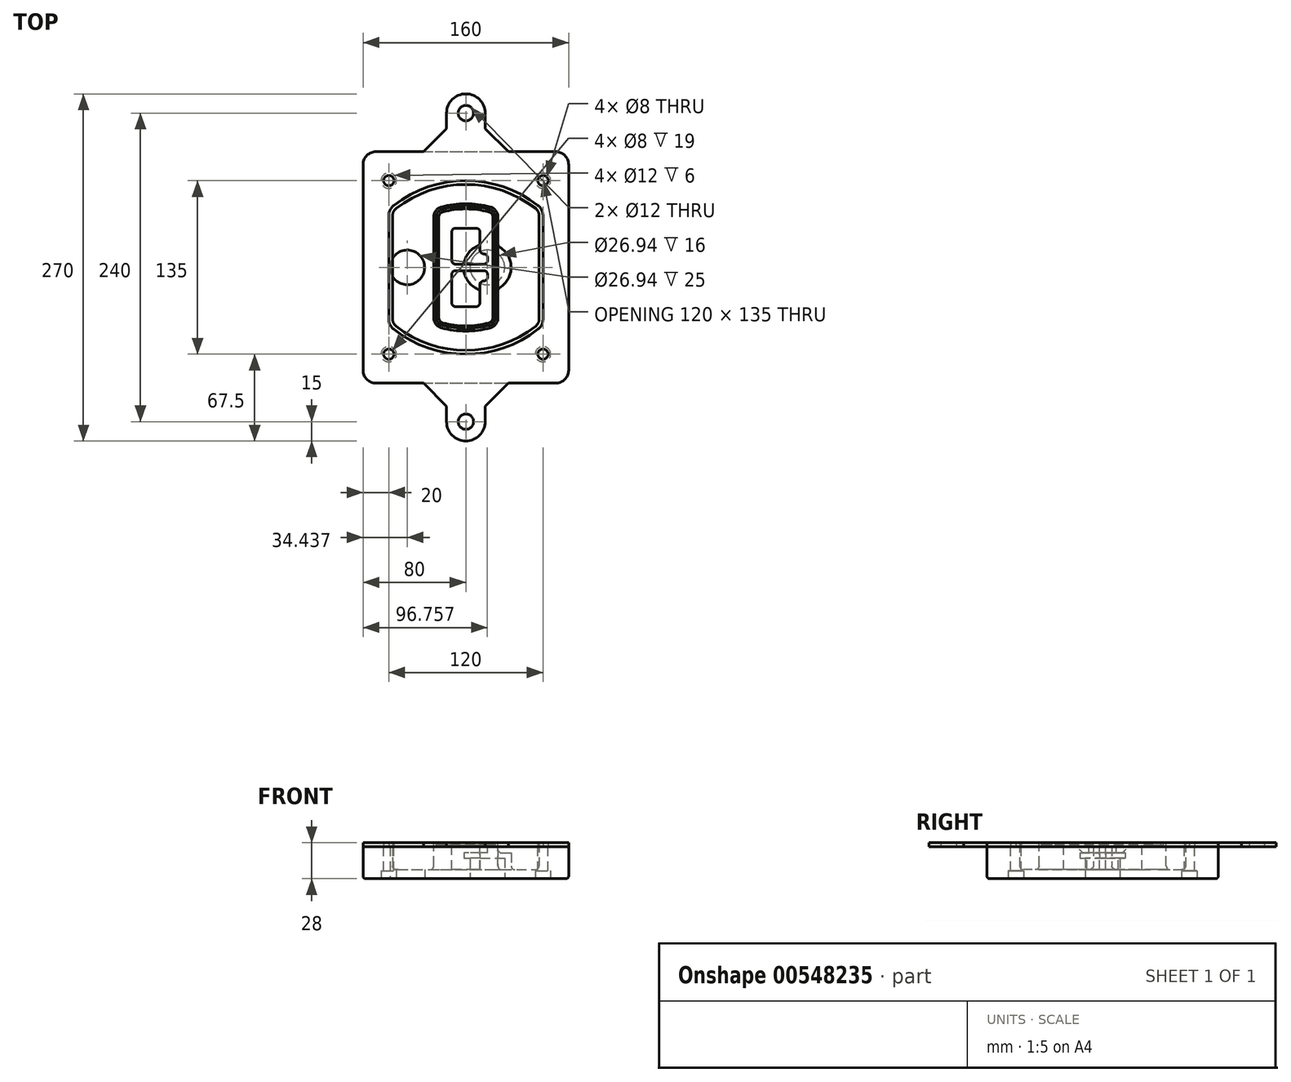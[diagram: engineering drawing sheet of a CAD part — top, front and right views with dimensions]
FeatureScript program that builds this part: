
annotation { "Feature Type Name" : "Feature", "Feature Type Description" : "" }
export const myFeature = defineFeature(function(context is Context, id is Id, definition is map)
    precondition{}
    {
        {
            var Q0;
            Q0=qCreatedBy(makeId("Top.planeOp"),FACE);
            var sketch = newSketch(context, id + "F0", { "sketchPlane" : qUnion([Q0])});
            skPoint(sketch, "E0.rect.middle", {"position": v(0, 0) * mm});
            skLineSegment(sketch, "E1.bottom", {"start": v(-70, -90) * mm, "end": v(70, -90) * mm});
            skLineSegment(sketch, "E1.top", {"start": v(-70, 90) * mm, "end": v(70, 90) * mm});
            skLineSegment(sketch, "E1.left", {"start": v(-80, -80) * mm, "end": v(-80, 80) * mm});
            skLineSegment(sketch, "E1.right", {"start": v(80, -80) * mm, "end": v(80, 80) * mm});
            skLineSegment(sketch, "E2", {"start": v(-80, 90) * mm, "end": v(80, -90) * mm, "construction": true});
            skLineSegment(sketch, "E3", {"start": v(80, 90) * mm, "end": v(-80, -90) * mm, "construction": true});
            skCircle(sketch, "E4", {"center": v(-60, 67.5) * mm, "radius": 4 * mm});
            skCircle(sketch, "E5", {"center": v(60, 67.5) * mm, "radius": 4 * mm});
            skCircle(sketch, "E6", {"center": v(60, -67.5) * mm, "radius": 4 * mm});
            skCircle(sketch, "E7", {"center": v(-60, -67.5) * mm, "radius": 4 * mm});
            skLineSegment(sketch, "E8", {"start": v(-60, 67.5) * mm, "end": v(60, 67.5) * mm, "construction": true});
            skLineSegment(sketch, "E9", {"start": v(60, 67.5) * mm, "end": v(60, -67.5) * mm, "construction": true});
            skLineSegment(sketch, "E10", {"start": v(60, -67.5) * mm, "end": v(-60, -67.5) * mm, "construction": true});
            skLineSegment(sketch, "E11", {"start": v(-60, -67.5) * mm, "end": v(-60, 67.5) * mm, "construction": true});
            skLineSegment(sketch, "E12", {"start": v(-60, 40.3) * mm, "end": v(-60, -40.3) * mm});
            skLineSegment(sketch, "E13", {"start": v(60, 40.3) * mm, "end": v(60, -40.3) * mm});
            skArc(sketch, "E14", {"start": v(56.15, 48.18) * mm, "mid": v(0, 67.5) * mm, "end": v(-56.15, 48.18) * mm});
            skArc(sketch, "E15", {"start": v(-56.15, -48.18) * mm, "mid": v(0, -67.5) * mm, "end": v(56.15, -48.18) * mm});
            skLineSegment(sketch, "E16", {"start": v(-60, 0) * mm, "end": v(60, 0) * mm, "construction": true});
            skPoint(sketch, "E17.visualSharp", {"position": v(-60, -45) * mm});
            skArc(sketch, "E17.filletArc", {"start": v(-60, -40.3) * mm, "mid": v(-58.99, -44.68) * mm, "end": v(-56.15, -48.18) * mm});
            skPoint(sketch, "E18.visualSharp", {"position": v(-60, 45) * mm});
            skArc(sketch, "E18.filletArc", {"start": v(-56.15, 48.18) * mm, "mid": v(-58.99, 44.68) * mm, "end": v(-60, 40.3) * mm});
            skPoint(sketch, "E19.visualSharp", {"position": v(60, 45) * mm});
            skArc(sketch, "E19.filletArc", {"start": v(60, 40.3) * mm, "mid": v(58.99, 44.68) * mm, "end": v(56.15, 48.18) * mm});
            skPoint(sketch, "E20.visualSharp", {"position": v(60, -45) * mm});
            skArc(sketch, "E20.filletArc", {"start": v(56.15, -48.18) * mm, "mid": v(58.99, -44.68) * mm, "end": v(60, -40.3) * mm});
            skPoint(sketch, "E21.visualSharp", {"position": v(-80, 90) * mm});
            skArc(sketch, "E21.filletArc", {"start": v(-70, 90) * mm, "mid": v(-77.07, 87.07) * mm, "end": v(-80, 80) * mm});
            skPoint(sketch, "E22.visualSharp", {"position": v(80, 90) * mm});
            skArc(sketch, "E22.filletArc", {"start": v(80, 80) * mm, "mid": v(77.07, 87.07) * mm, "end": v(70, 90) * mm});
            skPoint(sketch, "E23.visualSharp", {"position": v(80, -90) * mm});
            skArc(sketch, "E23.filletArc", {"start": v(70, -90) * mm, "mid": v(77.07, -87.07) * mm, "end": v(80, -80) * mm});
            skPoint(sketch, "E24.visualSharp", {"position": v(-80, -90) * mm});
            skArc(sketch, "E24.filletArc", {"start": v(-80, -80) * mm, "mid": v(-77.07, -87.07) * mm, "end": v(-70, -90) * mm});
            skArc(sketch, "E25.0", {"start": v(57, 40.3) * mm, "mid": v(56.3, 43.36) * mm, "end": v(54.3, 45.81) * mm});
            skLineSegment(sketch, "E25.1", {"start": v(57, 40.3) * mm, "end": v(57, -40.3) * mm});
            skArc(sketch, "E25.2", {"start": v(54.3, -45.81) * mm, "mid": v(56.3, -43.36) * mm, "end": v(57, -40.3) * mm});
            skArc(sketch, "E25.3", {"start": v(-54.3, -45.81) * mm, "mid": v(0, -64.5) * mm, "end": v(54.3, -45.81) * mm});
            skArc(sketch, "E25.4", {"start": v(-57, -40.3) * mm, "mid": v(-56.3, -43.36) * mm, "end": v(-54.3, -45.81) * mm});
            skArc(sketch, "E25.5", {"start": v(54.3, 45.81) * mm, "mid": v(0, 64.5) * mm, "end": v(-54.3, 45.81) * mm});
            skLineSegment(sketch, "E25.6", {"start": v(-57, 40.3) * mm, "end": v(-57, -40.3) * mm});
            skArc(sketch, "E25.7", {"start": v(-54.3, 45.81) * mm, "mid": v(-56.3, 43.36) * mm, "end": v(-57, 40.3) * mm});
            skArc(sketch, "E26.0", {"start": v(-58.62, 51.33) * mm, "mid": v(-62.58, 46.43) * mm, "end": v(-64, 40.3) * mm});
            skArc(sketch, "E26.1", {"start": v(58.62, 51.33) * mm, "mid": v(0, 71.5) * mm, "end": v(-58.62, 51.33) * mm});
            skArc(sketch, "E26.2", {"start": v(64, 40.3) * mm, "mid": v(62.58, 46.43) * mm, "end": v(58.62, 51.33) * mm});
            skLineSegment(sketch, "E26.3", {"start": v(64, 40.3) * mm, "end": v(64, -40.3) * mm});
            skArc(sketch, "E26.4", {"start": v(58.62, -51.33) * mm, "mid": v(62.58, -46.43) * mm, "end": v(64, -40.3) * mm});
            skLineSegment(sketch, "E26.5", {"start": v(-64, 40.3) * mm, "end": v(-64, -40.3) * mm});
            skArc(sketch, "E26.6", {"start": v(-58.62, -51.33) * mm, "mid": v(0, -71.5) * mm, "end": v(58.62, -51.33) * mm});
            skArc(sketch, "E26.7", {"start": v(-64, -40.3) * mm, "mid": v(-62.58, -46.43) * mm, "end": v(-58.62, -51.33) * mm});
            skSolve(sketch);
        }
        {
            var Q0;
            Q0=makeQuery(id+"F0.imprint","IMPRINT",FACE,{"disambiguationData":[TD([[makeQuery(id+"F0.imprint","IMPRINT",EDGE,{"derivedFrom":sQuery(id+"F0.wireOp",EDGE,"E1.bottom")}),1.0]])]});
            var Q1;
            Q1=makeQuery(id+"F0.imprint","IMPRINT",FACE,{"disambiguationData":[TD([[makeQuery(id+"F0.imprint","IMPRINT",EDGE,{"derivedFrom":sQuery(id+"F0.wireOp",EDGE,"E12")}),1.0]])]});
            var Q2;
            Q2=makeQuery(id+"F0.imprint","IMPRINT",FACE,{"disambiguationData":[TD([[makeQuery(id+"F0.imprint","IMPRINT",EDGE,{"derivedFrom":sQuery(id+"F0.wireOp",EDGE,"E25.0")}),1.0]])]});
            var Q3;
            Q3=makeQuery(id+"F0.imprint","IMPRINT",FACE,{"disambiguationData":[TD([[makeQuery(id+"F0.imprint","IMPRINT",EDGE,{"derivedFrom":sQuery(id+"F0.wireOp",EDGE,"E12")}),-1.0]])]});
            extrude(context, id + "F1", {"entities" : qUnion([Q0, Q1, Q2, Q3]), "oppositeDirection" : true, "depth" : 25 * mm});
        }
        {
            var Q0;
            Q0=makeQuery(id+"F0.imprint","IMPRINT",FACE,{"disambiguationData":[TD([[makeQuery(id+"F0.imprint","IMPRINT",EDGE,{"derivedFrom":sQuery(id+"F0.wireOp",EDGE,"E12")}),1.0]])]});
            extrude(context, id + "F2", {"entities" : qUnion([Q0]), "operationType" : NewBodyOperationType.ADD, "depth" : 3 * mm});
        }
        {
            var Q0;
            Q0=makeQuery(id+"F0.imprint","IMPRINT",FACE,{"disambiguationData":[TD([[makeQuery(id+"F0.imprint","IMPRINT",EDGE,{"derivedFrom":sQuery(id+"F0.wireOp",EDGE,"E25.0")}),1.0]])]});
            extrude(context, id + "F3", {"entities" : qUnion([Q0]), "operationType" : NewBodyOperationType.REMOVE, "oppositeDirection" : true, "depth" : 18 * mm});
        }
        {
            var Q0;
            Q0=makeQuery(id+"F2.opExtrude","CAP_FACE",FACE,{"disambiguationData":[OSD([sQuery(id+"F0.wireOp",EDGE,"E12"),sQuery(id+"F0.wireOp",EDGE,"E13"),sQuery(id+"F0.wireOp",EDGE,"E14"),sQuery(id+"F0.wireOp",EDGE,"E15"),sQuery(id+"F0.wireOp",EDGE,"E17.filletArc"),sQuery(id+"F0.wireOp",EDGE,"E18.filletArc"),sQuery(id+"F0.wireOp",EDGE,"E19.filletArc"),sQuery(id+"F0.wireOp",EDGE,"E20.filletArc"),sQuery(id+"F0.wireOp",EDGE,"E25.0"),sQuery(id+"F0.wireOp",EDGE,"E25.1"),sQuery(id+"F0.wireOp",EDGE,"E25.2"),sQuery(id+"F0.wireOp",EDGE,"E25.3"),sQuery(id+"F0.wireOp",EDGE,"E25.4"),sQuery(id+"F0.wireOp",EDGE,"E25.5"),sQuery(id+"F0.wireOp",EDGE,"E25.6"),sQuery(id+"F0.wireOp",EDGE,"E25.7")])],"isStart":false});
            var sketch = newSketch(context, id + "F4", { "sketchPlane" : qUnion([Q0])});
            skArc(sketch, "E27.0", {"start": v(-19.08, -46.97) * mm, "mid": v(0, -49.5) * mm, "end": v(19.08, -46.97) * mm});
            skArc(sketch, "E28.0", {"start": v(19.08, 46.97) * mm, "mid": v(0, 49.5) * mm, "end": v(-19.08, 46.97) * mm});
            skLineSegment(sketch, "E29", {"start": v(-25, 39.25) * mm, "end": v(-25, -39.25) * mm});
            skLineSegment(sketch, "E30", {"start": v(25, 39.25) * mm, "end": v(25, -39.25) * mm});
            skLineSegment(sketch, "E31", {"start": v(-25, 45.1) * mm, "end": v(25, 45.1) * mm, "construction": true});
            skLineSegment(sketch, "E32", {"start": v(-25, -45.1) * mm, "end": v(25, -45.1) * mm, "construction": true});
            skPoint(sketch, "E33.visualSharp", {"position": v(-25, 45.1) * mm});
            skArc(sketch, "E33.filletArc", {"start": v(-19.08, 46.97) * mm, "mid": v(-23.35, 44.11) * mm, "end": v(-25, 39.25) * mm});
            skPoint(sketch, "E34.visualSharp", {"position": v(25, 45.1) * mm});
            skArc(sketch, "E34.filletArc", {"start": v(25, 39.25) * mm, "mid": v(23.35, 44.11) * mm, "end": v(19.08, 46.97) * mm});
            skPoint(sketch, "E35.visualSharp", {"position": v(25, -45.1) * mm});
            skArc(sketch, "E35.filletArc", {"start": v(19.08, -46.97) * mm, "mid": v(23.35, -44.11) * mm, "end": v(25, -39.25) * mm});
            skPoint(sketch, "E36.visualSharp", {"position": v(-25, -45.1) * mm});
            skArc(sketch, "E36.filletArc", {"start": v(-25, -39.25) * mm, "mid": v(-23.35, -44.11) * mm, "end": v(-19.08, -46.97) * mm});
            skArc(sketch, "E37.0", {"start": v(54.3, 45.81) * mm, "mid": v(0, 64.5) * mm, "end": v(-54.3, 45.81) * mm});
            skArc(sketch, "E37.1", {"start": v(-54.3, 45.81) * mm, "mid": v(-56.3, 43.36) * mm, "end": v(-57, 40.3) * mm});
            skLineSegment(sketch, "E37.2", {"start": v(-57, 40.3) * mm, "end": v(-57, -40.3) * mm});
            skArc(sketch, "E37.3", {"start": v(-57, -40.3) * mm, "mid": v(-56.3, -43.36) * mm, "end": v(-54.3, -45.81) * mm});
            skArc(sketch, "E37.4", {"start": v(-54.3, -45.81) * mm, "mid": v(0, -64.5) * mm, "end": v(54.3, -45.81) * mm});
            skArc(sketch, "E37.5", {"start": v(54.3, -45.81) * mm, "mid": v(56.3, -43.36) * mm, "end": v(57, -40.3) * mm});
            skLineSegment(sketch, "E37.6", {"start": v(57, 40.3) * mm, "end": v(57, -40.3) * mm});
            skArc(sketch, "E37.7", {"start": v(57, 40.3) * mm, "mid": v(56.3, 43.36) * mm, "end": v(54.3, 45.81) * mm});
            skLineSegment(sketch, "E38.0", {"start": v(23, 39.25) * mm, "end": v(23, -39.25) * mm});
            skArc(sketch, "E38.1", {"start": v(18.56, -45.04) * mm, "mid": v(21.76, -42.9) * mm, "end": v(23, -39.25) * mm});
            skArc(sketch, "E38.2", {"start": v(-18.56, -45.04) * mm, "mid": v(0, -47.5) * mm, "end": v(18.56, -45.04) * mm});
            skArc(sketch, "E38.3", {"start": v(-23, -39.25) * mm, "mid": v(-21.76, -42.9) * mm, "end": v(-18.56, -45.04) * mm});
            skLineSegment(sketch, "E38.4", {"start": v(-23, 39.25) * mm, "end": v(-23, -39.25) * mm});
            skArc(sketch, "E38.5", {"start": v(23, 39.25) * mm, "mid": v(21.76, 42.9) * mm, "end": v(18.56, 45.04) * mm});
            skArc(sketch, "E38.6", {"start": v(-18.56, 45.04) * mm, "mid": v(-21.76, 42.9) * mm, "end": v(-23, 39.25) * mm});
            skArc(sketch, "E38.7", {"start": v(18.56, 45.04) * mm, "mid": v(0, 47.5) * mm, "end": v(-18.56, 45.04) * mm});
            skArc(sketch, "E39.0", {"start": v(21, 39.25) * mm, "mid": v(20.18, 41.68) * mm, "end": v(18.04, 43.1) * mm});
            skLineSegment(sketch, "E39.1", {"start": v(21, 39.25) * mm, "end": v(21, -39.25) * mm});
            skArc(sketch, "E39.2", {"start": v(18.04, -43.1) * mm, "mid": v(20.18, -41.68) * mm, "end": v(21, -39.25) * mm});
            skArc(sketch, "E39.3", {"start": v(-18.04, -43.1) * mm, "mid": v(0, -45.5) * mm, "end": v(18.04, -43.1) * mm});
            skArc(sketch, "E39.4", {"start": v(-21, -39.25) * mm, "mid": v(-20.18, -41.68) * mm, "end": v(-18.04, -43.1) * mm});
            skArc(sketch, "E39.5", {"start": v(18.04, 43.1) * mm, "mid": v(0, 45.5) * mm, "end": v(-18.04, 43.1) * mm});
            skLineSegment(sketch, "E39.6", {"start": v(-21, 39.25) * mm, "end": v(-21, -39.25) * mm});
            skArc(sketch, "E39.7", {"start": v(-18.04, 43.1) * mm, "mid": v(-20.18, 41.68) * mm, "end": v(-21, 39.25) * mm});
            skLineSegment(sketch, "E40", {"start": v(-25, 0) * mm, "end": v(25, 0) * mm, "construction": true});
            skLineSegment(sketch, "E41", {"start": v(-11, 5.5) * mm, "end": v(-11, 27.5) * mm});
            skLineSegment(sketch, "E42", {"start": v(-8, 30.5) * mm, "end": v(8, 30.5) * mm});
            skLineSegment(sketch, "E43", {"start": v(11, 27.5) * mm, "end": v(11, 13.5) * mm});
            skLineSegment(sketch, "E44", {"start": v(14, 10.5) * mm, "end": v(14, 10.5) * mm});
            skLineSegment(sketch, "E45", {"start": v(17, 7.5) * mm, "end": v(17, 5.5) * mm});
            skLineSegment(sketch, "E46", {"start": v(14, 2.5) * mm, "end": v(-8, 2.5) * mm});
            skPoint(sketch, "E47.visualSharp", {"position": v(-11, 30.5) * mm});
            skArc(sketch, "E47.filletArc", {"start": v(-8, 30.5) * mm, "mid": v(-10.12, 29.62) * mm, "end": v(-11, 27.5) * mm});
            skPoint(sketch, "E48.visualSharp", {"position": v(11, 30.5) * mm});
            skArc(sketch, "E48.filletArc", {"start": v(11, 27.5) * mm, "mid": v(10.12, 29.62) * mm, "end": v(8, 30.5) * mm});
            skPoint(sketch, "E49.visualSharp", {"position": v(11, 10.5) * mm});
            skArc(sketch, "E49.filletArc", {"start": v(11, 13.5) * mm, "mid": v(11.88, 11.38) * mm, "end": v(14, 10.5) * mm});
            skPoint(sketch, "E50.visualSharp", {"position": v(17, 10.5) * mm});
            skArc(sketch, "E50.filletArc", {"start": v(17, 7.5) * mm, "mid": v(16.12, 9.62) * mm, "end": v(14, 10.5) * mm});
            skPoint(sketch, "E51.visualSharp", {"position": v(17, 2.5) * mm});
            skArc(sketch, "E51.filletArc", {"start": v(14, 2.5) * mm, "mid": v(16.12, 3.38) * mm, "end": v(17, 5.5) * mm});
            skPoint(sketch, "E52.visualSharp", {"position": v(-11, 2.5) * mm});
            skArc(sketch, "E52.filletArc", {"start": v(-11, 5.5) * mm, "mid": v(-10.12, 3.38) * mm, "end": v(-8, 2.5) * mm});
            skLineSegment(sketch, "E53.0.MirrorCS", {"start": v(14, -2.5) * mm, "end": v(-8, -2.5) * mm});
            skArc(sketch, "E54.0.MirrorCS", {"start": v(-11, -5.5) * mm, "mid": v(-10.12, -3.38) * mm, "end": v(-8, -2.5) * mm});
            skLineSegment(sketch, "E55.0.MirrorCS", {"start": v(-11, -5.5) * mm, "end": v(-11, -27.5) * mm});
            skArc(sketch, "E56.0.MirrorCS", {"start": v(-8, -30.5) * mm, "mid": v(-10.12, -29.62) * mm, "end": v(-11, -27.5) * mm});
            skLineSegment(sketch, "E57.0.MirrorCS", {"start": v(-8, -30.5) * mm, "end": v(8, -30.5) * mm});
            skArc(sketch, "E58.0.MirrorCS", {"start": v(11, -27.5) * mm, "mid": v(10.12, -29.62) * mm, "end": v(8, -30.5) * mm});
            skLineSegment(sketch, "E59.0.MirrorCS", {"start": v(11, -27.5) * mm, "end": v(11, -13.5) * mm});
            skArc(sketch, "E60.0.MirrorCS", {"start": v(11, -13.5) * mm, "mid": v(11.88, -11.38) * mm, "end": v(14, -10.5) * mm});
            skArc(sketch, "E61.0.MirrorCS", {"start": v(17, -7.5) * mm, "mid": v(16.12, -9.62) * mm, "end": v(14, -10.5) * mm});
            skLineSegment(sketch, "E62.0.MirrorCS", {"start": v(17, -7.5) * mm, "end": v(17, -5.5) * mm});
            skArc(sketch, "E63.0.MirrorCS", {"start": v(14, -2.5) * mm, "mid": v(16.12, -3.38) * mm, "end": v(17, -5.5) * mm});
            skSolve(sketch);
        }
        {
            var Q0;
            Q0=makeQuery(id+"F4.imprint","IMPRINT",FACE,{"disambiguationData":[TD([[makeQuery(id+"F4.imprint","IMPRINT",EDGE,{"derivedFrom":sQuery(id+"F4.wireOp",EDGE,"E27.0")}),1.0]])]});
            var Q1;
            Q1=makeQuery(id+"F4.imprint","IMPRINT",FACE,{"disambiguationData":[TD([[makeQuery(id+"F4.imprint","IMPRINT",EDGE,{"derivedFrom":sQuery(id+"F4.wireOp",EDGE,"E38.0")}),-1.0]])]});
            var Q2;
            Q2=makeQuery(id+"F4.imprint","IMPRINT",FACE,{"disambiguationData":[TD([[makeQuery(id+"F4.imprint","IMPRINT",EDGE,{"derivedFrom":sQuery(id+"F4.wireOp",EDGE,"E39.0")}),1.0]])]});
            extrude(context, id + "F5", {"entities" : qUnion([Q0, Q1, Q2]), "operationType" : NewBodyOperationType.ADD, "endBound" : BoundingType.UP_TO_NEXT, "oppositeDirection" : true, "depth" : 25 * mm});
        }
        {
            var Q0;
            Q0=makeQuery(id+"F4.imprint","IMPRINT",FACE,{"disambiguationData":[TD([[makeQuery(id+"F4.imprint","IMPRINT",EDGE,{"derivedFrom":sQuery(id+"F4.wireOp",EDGE,"E38.0")}),-1.0]])]});
            extrude(context, id + "F6", {"entities" : qUnion([Q0]), "operationType" : NewBodyOperationType.REMOVE, "oppositeDirection" : true, "depth" : 2 * mm});
        }
        {
            var Q0;
            Q0=makeQuery(id+"F1.opExtrude","CAP_FACE",FACE,{"disambiguationData":[OSD([sQuery(id+"F0.wireOp",EDGE,"E1.bottom"),sQuery(id+"F0.wireOp",EDGE,"E1.top"),sQuery(id+"F0.wireOp",EDGE,"E1.left"),sQuery(id+"F0.wireOp",EDGE,"E1.right"),sQuery(id+"F0.wireOp",EDGE,"E4"),sQuery(id+"F0.wireOp",EDGE,"E5"),sQuery(id+"F0.wireOp",EDGE,"E6"),sQuery(id+"F0.wireOp",EDGE,"E7"),sQuery(id+"F0.wireOp",EDGE,"E21.filletArc"),sQuery(id+"F0.wireOp",EDGE,"E22.filletArc"),sQuery(id+"F0.wireOp",EDGE,"E23.filletArc"),sQuery(id+"F0.wireOp",EDGE,"E24.filletArc")])],"isStart":false});
            var sketch = newSketch(context, id + "F7", { "sketchPlane" : qUnion([Q0])});
            skCircle(sketch, "E64", {"center": v(16.76, 0) * mm, "radius": 13.47 * mm});
            skCircle(sketch, "E65", {"center": v(-45.56, 0) * mm, "radius": 13.47 * mm});
            skLineSegment(sketch, "E66", {"start": v(80, 0) * mm, "end": v(-80, 0) * mm});
            skCircle(sketch, "E67", {"center": v(16.76, 0) * mm, "radius": 18.47 * mm});
            skCircle(sketch, "E68", {"center": v(60, -67.5) * mm, "radius": 6 * mm});
            skCircle(sketch, "E69", {"center": v(-60, -67.5) * mm, "radius": 6 * mm});
            skCircle(sketch, "E70", {"center": v(-60, 67.5) * mm, "radius": 6 * mm});
            skCircle(sketch, "E71", {"center": v(60, 67.5) * mm, "radius": 6 * mm});
            skSolve(sketch);
        }
        {
            var Q0;
            {var subQ1=sQuery(id+"F7.wireOp",EDGE,"E66");var subQ4=sQuery(id+"F7.wireOp",EDGE,"E64");var subQ6=makeQuery(id+"F7.imprint","INTERSECT",VERTEX,{"disambiguationData":[OD(0.0)],"derivedFrom":[subQ4,subQ1]});Q0=makeQuery(id+"F7.imprint","IMPRINT",FACE,{"disambiguationData":[TD([[makeQuery(id+"F7.imprint","IMPRINT",EDGE,{"disambiguationData":[TD([[subQ6,-1.0]])],"derivedFrom":subQ4}),-1.0]])]});}
            var Q1;
            {var subQ0=sQuery(id+"F7.wireOp",EDGE,"E66");var subQ1=sQuery(id+"F7.wireOp",EDGE,"E64");var subQ3=makeQuery(id+"F7.imprint","INTERSECT",VERTEX,{"disambiguationData":[OD(0.0)],"derivedFrom":[subQ1,subQ0]});Q1=makeQuery(id+"F7.imprint","IMPRINT",FACE,{"disambiguationData":[TD([[makeQuery(id+"F7.imprint","IMPRINT",EDGE,{"disambiguationData":[TD([[subQ3,-1.0]])],"derivedFrom":subQ1}),1.0]])]});}
            var Q2;
            {var subQ0=sQuery(id+"F7.wireOp",EDGE,"E66");var subQ1=sQuery(id+"F7.wireOp",EDGE,"E64");var subQ3=makeQuery(id+"F7.imprint","INTERSECT",VERTEX,{"disambiguationData":[OD(0.0)],"derivedFrom":[subQ1,subQ0]});Q2=makeQuery(id+"F7.imprint","IMPRINT",FACE,{"disambiguationData":[TD([[makeQuery(id+"F7.imprint","IMPRINT",EDGE,{"disambiguationData":[TD([[subQ3,1.0]])],"derivedFrom":subQ1}),1.0]])]});}
            var Q3;
            {var subQ1=sQuery(id+"F7.wireOp",EDGE,"E66");var subQ4=sQuery(id+"F7.wireOp",EDGE,"E64");var subQ6=makeQuery(id+"F7.imprint","INTERSECT",VERTEX,{"disambiguationData":[OD(0.0)],"derivedFrom":[subQ4,subQ1]});Q3=makeQuery(id+"F7.imprint","IMPRINT",FACE,{"disambiguationData":[TD([[makeQuery(id+"F7.imprint","IMPRINT",EDGE,{"disambiguationData":[TD([[subQ6,1.0]])],"derivedFrom":subQ4}),-1.0]])]});}
            extrude(context, id + "F8", {"entities" : qUnion([Q0, Q1, Q2, Q3]), "operationType" : NewBodyOperationType.ADD, "oppositeDirection" : true, "depth" : 20 * mm});
        }
        {
            var Q0;
            {var subQ0=sQuery(id+"F7.wireOp",EDGE,"E66");var subQ1=sQuery(id+"F7.wireOp",EDGE,"E64");var subQ3=makeQuery(id+"F7.imprint","INTERSECT",VERTEX,{"disambiguationData":[OD(0.0)],"derivedFrom":[subQ1,subQ0]});Q0=makeQuery(id+"F7.imprint","IMPRINT",FACE,{"disambiguationData":[TD([[makeQuery(id+"F7.imprint","IMPRINT",EDGE,{"disambiguationData":[TD([[subQ3,-1.0]])],"derivedFrom":subQ1}),1.0]])]});}
            var Q1;
            {var subQ0=sQuery(id+"F7.wireOp",EDGE,"E66");var subQ1=sQuery(id+"F7.wireOp",EDGE,"E64");var subQ3=makeQuery(id+"F7.imprint","INTERSECT",VERTEX,{"disambiguationData":[OD(0.0)],"derivedFrom":[subQ1,subQ0]});Q1=makeQuery(id+"F7.imprint","IMPRINT",FACE,{"disambiguationData":[TD([[makeQuery(id+"F7.imprint","IMPRINT",EDGE,{"disambiguationData":[TD([[subQ3,1.0]])],"derivedFrom":subQ1}),1.0]])]});}
            extrude(context, id + "F9", {"entities" : qUnion([Q0, Q1]), "operationType" : NewBodyOperationType.REMOVE, "oppositeDirection" : true, "depth" : 16 * mm});
        }
        {
            var Q0;
            {var subQ0=sQuery(id+"F7.wireOp",EDGE,"E66");var subQ1=sQuery(id+"F7.wireOp",EDGE,"E65");var subQ3=makeQuery(id+"F7.imprint","INTERSECT",VERTEX,{"disambiguationData":[OD(0.0)],"derivedFrom":[subQ1,subQ0]});Q0=makeQuery(id+"F7.imprint","IMPRINT",FACE,{"disambiguationData":[TD([[makeQuery(id+"F7.imprint","IMPRINT",EDGE,{"disambiguationData":[TD([[subQ3,-1.0]])],"derivedFrom":subQ1}),1.0]])]});}
            var Q1;
            {var subQ0=sQuery(id+"F7.wireOp",EDGE,"E66");var subQ1=sQuery(id+"F7.wireOp",EDGE,"E65");var subQ3=makeQuery(id+"F7.imprint","INTERSECT",VERTEX,{"disambiguationData":[OD(0.0)],"derivedFrom":[subQ1,subQ0]});Q1=makeQuery(id+"F7.imprint","IMPRINT",FACE,{"disambiguationData":[TD([[makeQuery(id+"F7.imprint","IMPRINT",EDGE,{"disambiguationData":[TD([[subQ3,1.0]])],"derivedFrom":subQ1}),1.0]])]});}
            extrude(context, id + "F10", {"entities" : qUnion([Q0, Q1]), "operationType" : NewBodyOperationType.REMOVE, "oppositeDirection" : true, "depth" : 25 * mm});
        }
        {
            var Q0;
            Q0=makeQuery(id+"F7.imprint","IMPRINT",FACE,{"disambiguationData":[TD([[makeQuery(id+"F7.imprint","IMPRINT",EDGE,{"derivedFrom":sQuery(id+"F7.wireOp",EDGE,"E68")}),1.0]])]});
            var Q1;
            Q1=makeQuery(id+"F7.imprint","IMPRINT",FACE,{"disambiguationData":[TD([[makeQuery(id+"F7.imprint","IMPRINT",EDGE,{"derivedFrom":makeQuery(id+"F1.opExtrude","CAP_EDGE",EDGE,{"disambiguationData":[OSD([sQuery(id+"F0.wireOp",EDGE,"E5")])],"isStart":false})}),-1.0]])]});
            var Q2;
            Q2=makeQuery(id+"F7.imprint","IMPRINT",FACE,{"disambiguationData":[TD([[makeQuery(id+"F7.imprint","IMPRINT",EDGE,{"derivedFrom":sQuery(id+"F7.wireOp",EDGE,"E69")}),1.0]])]});
            var Q3;
            Q3=makeQuery(id+"F7.imprint","IMPRINT",FACE,{"disambiguationData":[TD([[makeQuery(id+"F7.imprint","IMPRINT",EDGE,{"derivedFrom":makeQuery(id+"F1.opExtrude","CAP_EDGE",EDGE,{"disambiguationData":[OSD([sQuery(id+"F0.wireOp",EDGE,"E4")])],"isStart":false})}),-1.0]])]});
            var Q4;
            Q4=makeQuery(id+"F7.imprint","IMPRINT",FACE,{"disambiguationData":[TD([[makeQuery(id+"F7.imprint","IMPRINT",EDGE,{"derivedFrom":sQuery(id+"F7.wireOp",EDGE,"E70")}),1.0]])]});
            var Q5;
            Q5=makeQuery(id+"F7.imprint","IMPRINT",FACE,{"disambiguationData":[TD([[makeQuery(id+"F7.imprint","IMPRINT",EDGE,{"derivedFrom":makeQuery(id+"F1.opExtrude","CAP_EDGE",EDGE,{"disambiguationData":[OSD([sQuery(id+"F0.wireOp",EDGE,"E7")])],"isStart":false})}),-1.0]])]});
            var Q6;
            Q6=makeQuery(id+"F7.imprint","IMPRINT",FACE,{"disambiguationData":[TD([[makeQuery(id+"F7.imprint","IMPRINT",EDGE,{"derivedFrom":sQuery(id+"F7.wireOp",EDGE,"E71")}),1.0]])]});
            var Q7;
            Q7=makeQuery(id+"F7.imprint","IMPRINT",FACE,{"disambiguationData":[TD([[makeQuery(id+"F7.imprint","IMPRINT",EDGE,{"derivedFrom":makeQuery(id+"F1.opExtrude","CAP_EDGE",EDGE,{"disambiguationData":[OSD([sQuery(id+"F0.wireOp",EDGE,"E6")])],"isStart":false})}),-1.0]])]});
            extrude(context, id + "F11", {"entities" : qUnion([Q0, Q1, Q2, Q3, Q4, Q5, Q6, Q7]), "operationType" : NewBodyOperationType.REMOVE, "oppositeDirection" : true, "depth" : 6 * mm});
        }
        {
            var Q0;
            Q0=makeQuery(id+"F9.boolean.opBoolean","COPY",FACE,{"derivedFrom":makeQuery(id+"F9.opExtrude","CAP_FACE",FACE,{"disambiguationData":[OSD([sQuery(id+"F7.wireOp",EDGE,"E64")])],"isStart":false})});
            var sketch = newSketch(context, id + "F12", { "sketchPlane" : qUnion([Q0])});
            skArc(sketch, "E72.0", {"start": v(11, 17.55) * mm, "mid": v(2.57, 11.82) * mm, "end": v(-1.54, 2.5) * mm});
            skArc(sketch, "E72.1", {"start": v(-1.54, -2.5) * mm, "mid": v(2.57, -11.82) * mm, "end": v(11, -17.55) * mm});
            skLineSegment(sketch, "E73", {"start": v(-1.54, -2.5) * mm, "end": v(14, -2.5) * mm});
            skLineSegment(sketch, "E74.0", {"start": v(14, 2.5) * mm, "end": v(-1.54, 2.5) * mm});
            skArc(sketch, "E74.1", {"start": v(14, 2.5) * mm, "mid": v(16.12, 3.38) * mm, "end": v(17, 5.5) * mm});
            skLineSegment(sketch, "E74.2", {"start": v(17, 7.5) * mm, "end": v(17, 5.5) * mm});
            skArc(sketch, "E74.3", {"start": v(17, 7.5) * mm, "mid": v(16.12, 9.62) * mm, "end": v(14, 10.5) * mm});
            skArc(sketch, "E74.4", {"start": v(11, 13.5) * mm, "mid": v(11.88, 11.38) * mm, "end": v(14, 10.5) * mm});
            skLineSegment(sketch, "E74.5", {"start": v(11, 17.55) * mm, "end": v(11, 13.5) * mm});
            skLineSegment(sketch, "E74.7", {"start": v(14, -2.5) * mm, "end": v(-1.54, -2.5) * mm});
            skArc(sketch, "E74.8", {"start": v(14, -2.5) * mm, "mid": v(16.12, -3.38) * mm, "end": v(17, -5.5) * mm});
            skLineSegment(sketch, "E74.9", {"start": v(17, -7.5) * mm, "end": v(17, -5.5) * mm});
            skArc(sketch, "E74.10", {"start": v(17, -7.5) * mm, "mid": v(16.12, -9.62) * mm, "end": v(14, -10.5) * mm});
            skArc(sketch, "E74.11", {"start": v(11, -13.5) * mm, "mid": v(11.88, -11.38) * mm, "end": v(14, -10.5) * mm});
            skLineSegment(sketch, "E74.12", {"start": v(11, -17.55) * mm, "end": v(11, -13.5) * mm});
            skPoint(sketch, "E75.orphan", {"position": v(11, -27.5) * mm});
            skPoint(sketch, "E76.orphan", {"position": v(-8, -2.5) * mm});
            skPoint(sketch, "E77.orphan", {"position": v(-8, 2.5) * mm});
            skPoint(sketch, "E78.orphan", {"position": v(11, 27.5) * mm});
            skSolve(sketch);
        }
        {
            var Q0;
            {var subQ7=sQuery(id+"F12.wireOp",EDGE,"E72.0");var subQ14=sQuery(id+"F12.wireOp",EDGE,"E72.1");var subQ16=sQuery(id+"F12.wireOp",EDGE,"E74.1");var subQ18=sQuery(id+"F12.wireOp",EDGE,"E74.8");Q0=qUnion([makeQuery(id+"F12.imprint","IMPRINT",FACE,{"disambiguationData":[TD([[makeQuery(id+"F12.imprint","IMPRINT",EDGE,{"derivedFrom":subQ7}),1.0]])]}),makeQuery(id+"F12.imprint","IMPRINT",FACE,{"disambiguationData":[TD([[makeQuery(id+"F12.imprint","IMPRINT",EDGE,{"derivedFrom":subQ14}),1.0]])]}),makeQuery(id+"F12.imprint","IMPRINT",FACE,{"disambiguationData":[TD([[makeQuery(id+"F12.imprint","IMPRINT",EDGE,{"derivedFrom":subQ16}),1.0]])]}),makeQuery(id+"F12.imprint","IMPRINT",FACE,{"disambiguationData":[TD([[makeQuery(id+"F12.imprint","IMPRINT",EDGE,{"derivedFrom":subQ18}),-1.0]])]})]);}
            var Q1;
            Q1=makeQuery(id+"F5.boolean.opBoolean","SPLIT",FACE,{"disambiguationData":[TD([makeQuery(id+"F5.opExtrude","SWEPT_FACE",FACE,{"disambiguationData":[OSD([sQuery(id+"F4.wireOp",EDGE,"E41")])]})])],"derivedFrom":makeQuery(id+"F3.boolean.opBoolean","COPY",FACE,{"derivedFrom":makeQuery(id+"F3.opExtrude","CAP_FACE",FACE,{"disambiguationData":[OSD([sQuery(id+"F0.wireOp",EDGE,"E25.0"),sQuery(id+"F0.wireOp",EDGE,"E25.1"),sQuery(id+"F0.wireOp",EDGE,"E25.2"),sQuery(id+"F0.wireOp",EDGE,"E25.3"),sQuery(id+"F0.wireOp",EDGE,"E25.4"),sQuery(id+"F0.wireOp",EDGE,"E25.5"),sQuery(id+"F0.wireOp",EDGE,"E25.6"),sQuery(id+"F0.wireOp",EDGE,"E25.7")])],"isStart":false})})});
            extrude(context, id + "F13", {"entities" : qUnion([Q0]), "operationType" : NewBodyOperationType.REMOVE, "endBound" : BoundingType.UP_TO_SURFACE, "endBoundEntityFace" : qUnion([Q1]), "depth" : 25 * mm});
        }
        {
            var Q0;
            Q0=makeQuery(id+"F3.boolean.opBoolean","COPY",EDGE,{"derivedFrom":makeQuery(id+"F3.opExtrude","CAP_EDGE",EDGE,{"disambiguationData":[OSD([sQuery(id+"F0.wireOp",EDGE,"E25.6")])],"isStart":false})});
            var Q1;
            Q1=makeQuery(id+"F8.boolean.opBoolean","INTERSECT",EDGE,{"derivedFrom":[makeQuery(id+"F5.opExtrude","SWEPT_FACE",FACE,{"disambiguationData":[OSD([sQuery(id+"F4.wireOp",EDGE,"E30")])]}),makeQuery(id+"F8.opExtrude","CAP_FACE",FACE,{"disambiguationData":[OSD([sQuery(id+"F7.wireOp",EDGE,"E67")])],"isStart":false})]});
            var Q2;
            Q2=makeQuery(id+"F8.boolean.opBoolean","INTERSECT",EDGE,{"disambiguationData":[OD(1.0)],"derivedFrom":[makeQuery(id+"F5.opExtrude","SWEPT_FACE",FACE,{"disambiguationData":[OSD([sQuery(id+"F4.wireOp",EDGE,"E30")])]}),makeQuery(id+"F8.opExtrude","SWEPT_FACE",FACE,{"disambiguationData":[OSD([sQuery(id+"F7.wireOp",EDGE,"E67")])]})]});
            var Q3;
            {var subQ0=sQuery(id+"F4.wireOp",EDGE,"E30");Q3=makeQuery(id+"F8.boolean.opBoolean","SPLIT",EDGE,{"disambiguationData":[TD([makeQuery(id+"F5.opExtrude","SWEPT_FACE",FACE,{"disambiguationData":[OSD([sQuery(id+"F4.wireOp",EDGE,"E35.filletArc")])]})])],"derivedFrom":makeQuery(id+"F5.opExtrude","CAP_EDGE",EDGE,{"disambiguationData":[OSD([subQ0])],"isStart":false})});}
            var Q4;
            {var subQ0=sQuery(id+"F0.wireOp",EDGE,"E25.7");var subQ1=sQuery(id+"F0.wireOp",EDGE,"E25.1");var subQ2=sQuery(id+"F0.wireOp",EDGE,"E25.6");var subQ3=sQuery(id+"F0.wireOp",EDGE,"E25.5");var subQ4=sQuery(id+"F0.wireOp",EDGE,"E25.4");var subQ5=sQuery(id+"F0.wireOp",EDGE,"E25.0");var subQ6=sQuery(id+"F0.wireOp",EDGE,"E25.2");var subQ7=sQuery(id+"F0.wireOp",EDGE,"E25.3");Q4=makeQuery(id+"F8.boolean.opBoolean","INTERSECT",EDGE,{"derivedFrom":[makeQuery(id+"F5.boolean.opBoolean","SPLIT",FACE,{"disambiguationData":[TD([makeQuery(id+"F2.opExtrude","SWEPT_FACE",FACE,{"disambiguationData":[OSD([subQ5])]})])],"derivedFrom":makeQuery(id+"F3.boolean.opBoolean","COPY",FACE,{"derivedFrom":makeQuery(id+"F3.opExtrude","CAP_FACE",FACE,{"disambiguationData":[OSD([subQ5,subQ1,subQ6,subQ7,subQ4,subQ3,subQ2,subQ0])],"isStart":false})})}),makeQuery(id+"F8.opExtrude","SWEPT_FACE",FACE,{"disambiguationData":[OSD([sQuery(id+"F7.wireOp",EDGE,"E67")])]})]});}
            var Q5;
            Q5=makeQuery(id+"F8.boolean.opBoolean","INTERSECT",EDGE,{"disambiguationData":[OD(0.0)],"derivedFrom":[makeQuery(id+"F5.opExtrude","SWEPT_FACE",FACE,{"disambiguationData":[OSD([sQuery(id+"F4.wireOp",EDGE,"E30")])]}),makeQuery(id+"F8.opExtrude","SWEPT_FACE",FACE,{"disambiguationData":[OSD([sQuery(id+"F7.wireOp",EDGE,"E67")])]})]});
            fillet(context, id + "F14", {"entities" : qUnion([Q0, Q1, Q2, Q3, Q4, Q5]), "radius" : 3 * mm, "tangentPropagation" : true, "allowEdgeOverflow" : false});
        }
        {
            var Q0;
            Q0=makeQuery(id+"F1.opExtrude","CAP_EDGE",EDGE,{"disambiguationData":[OSD([sQuery(id+"F0.wireOp",EDGE,"E1.bottom")])],"isStart":false});
            fillet(context, id + "F15", {"entities" : qUnion([Q0]), "radius" : 2 * mm, "tangentPropagation" : true, "allowEdgeOverflow" : false});
        }
        {
            var Q0;
            {var subQ0=sQuery(id+"F0.wireOp",EDGE,"E21.filletArc");var subQ1=sQuery(id+"F0.wireOp",EDGE,"E7");var subQ2=sQuery(id+"F0.wireOp",EDGE,"E6");var subQ3=sQuery(id+"F0.wireOp",EDGE,"E5");var subQ4=sQuery(id+"F0.wireOp",EDGE,"E4");var subQ5=sQuery(id+"F0.wireOp",EDGE,"E22.filletArc");var subQ6=sQuery(id+"F0.wireOp",EDGE,"E1.bottom");var subQ7=sQuery(id+"F0.wireOp",EDGE,"E1.right");var subQ8=sQuery(id+"F0.wireOp",EDGE,"E1.top");var subQ9=sQuery(id+"F0.wireOp",EDGE,"E1.left");var subQ10=sQuery(id+"F0.wireOp",EDGE,"E23.filletArc");var subQ11=sQuery(id+"F0.wireOp",EDGE,"E24.filletArc");Q0=makeQuery(id+"F2.boolean.opBoolean","SPLIT",FACE,{"disambiguationData":[TD([makeQuery(id+"F1.opExtrude","SWEPT_FACE",FACE,{"disambiguationData":[OSD([subQ6])]})])],"derivedFrom":makeQuery(id+"F1.opExtrude","CAP_FACE",FACE,{"disambiguationData":[OSD([subQ6,subQ8,subQ9,subQ7,subQ4,subQ3,subQ2,subQ1,subQ0,subQ5,subQ10,subQ11])],"isStart":true})});}
            var sketch = newSketch(context, id + "F16", { "sketchPlane" : qUnion([Q0])});
            skLineSegment(sketch, "E79", {"start": v(-33, 90) * mm, "end": v(-15, 108) * mm});
            skLineSegment(sketch, "E80", {"start": v(-15, 108) * mm, "end": v(-15, 120) * mm});
            skArc(sketch, "E81", {"start": v(15, 120) * mm, "mid": v(0, 135) * mm, "end": v(-15, 120) * mm});
            skLineSegment(sketch, "E82", {"start": v(15, 120) * mm, "end": v(15, 108) * mm});
            skLineSegment(sketch, "E83", {"start": v(15, 108) * mm, "end": v(33, 90) * mm});
            skCircle(sketch, "E84", {"center": v(0, 120) * mm, "radius": 6 * mm});
            skLineSegment(sketch, "E85", {"start": v(-80, 0) * mm, "end": v(80, 0) * mm, "construction": true});
            skLineSegment(sketch, "E86.MirrorCS", {"start": v(-33, -90) * mm, "end": v(-15, -108) * mm});
            skLineSegment(sketch, "E87.MirrorCS", {"start": v(-15, -108) * mm, "end": v(-15, -120) * mm});
            skArc(sketch, "E88.MirrorCS", {"start": v(15, -120) * mm, "mid": v(0, -135) * mm, "end": v(-15, -120) * mm});
            skCircle(sketch, "E89.MirrorC", {"center": v(0, -120) * mm, "radius": 6 * mm});
            skLineSegment(sketch, "E90.MirrorCS", {"start": v(15, -120) * mm, "end": v(15, -108) * mm});
            skLineSegment(sketch, "E91.MirrorCS", {"start": v(15, -108) * mm, "end": v(33, -90) * mm});
            skSolve(sketch);
        }
        {
            var Q0;
            {var subQ0=sQuery(id+"F16.wireOp",EDGE,"E79");Q0=makeQuery(id+"F16.imprint","IMPRINT",FACE,{"disambiguationData":[TD([[makeQuery(id+"F16.imprint","IMPRINT",EDGE,{"derivedFrom":subQ0}),-1.0]])]});}
            var Q1;
            Q1=makeQuery(id+"F16.imprint","IMPRINT",FACE,{"disambiguationData":[TD([[makeQuery(id+"F16.imprint","IMPRINT",EDGE,{"derivedFrom":makeQuery(id+"F1.opExtrude","CAP_EDGE",EDGE,{"disambiguationData":[OSD([sQuery(id+"F0.wireOp",EDGE,"E1.left")])],"isStart":true})}),-1.0]])]});
            var Q2;
            {var subQ0=sQuery(id+"F16.wireOp",EDGE,"E86.MirrorCS");Q2=makeQuery(id+"F16.imprint","IMPRINT",FACE,{"disambiguationData":[TD([[makeQuery(id+"F16.imprint","IMPRINT",EDGE,{"derivedFrom":subQ0}),1.0]])]});}
            var Q3;
            Q3=makeQuery(id+"F2.opExtrude","CAP_FACE",FACE,{"disambiguationData":[OSD([sQuery(id+"F0.wireOp",EDGE,"E12"),sQuery(id+"F0.wireOp",EDGE,"E13"),sQuery(id+"F0.wireOp",EDGE,"E14"),sQuery(id+"F0.wireOp",EDGE,"E15"),sQuery(id+"F0.wireOp",EDGE,"E17.filletArc"),sQuery(id+"F0.wireOp",EDGE,"E18.filletArc"),sQuery(id+"F0.wireOp",EDGE,"E19.filletArc"),sQuery(id+"F0.wireOp",EDGE,"E20.filletArc"),sQuery(id+"F0.wireOp",EDGE,"E25.0"),sQuery(id+"F0.wireOp",EDGE,"E25.1"),sQuery(id+"F0.wireOp",EDGE,"E25.2"),sQuery(id+"F0.wireOp",EDGE,"E25.3"),sQuery(id+"F0.wireOp",EDGE,"E25.4"),sQuery(id+"F0.wireOp",EDGE,"E25.5"),sQuery(id+"F0.wireOp",EDGE,"E25.6"),sQuery(id+"F0.wireOp",EDGE,"E25.7")])],"isStart":false});
            extrude(context, id + "F17", {"entities" : qUnion([Q0, Q1, Q2]), "endBound" : BoundingType.UP_TO_SURFACE, "depth" : 25 * mm, "endBoundEntityFace" : qUnion([Q3]), "offsetDistance" : 25 * mm});
        }
    });
